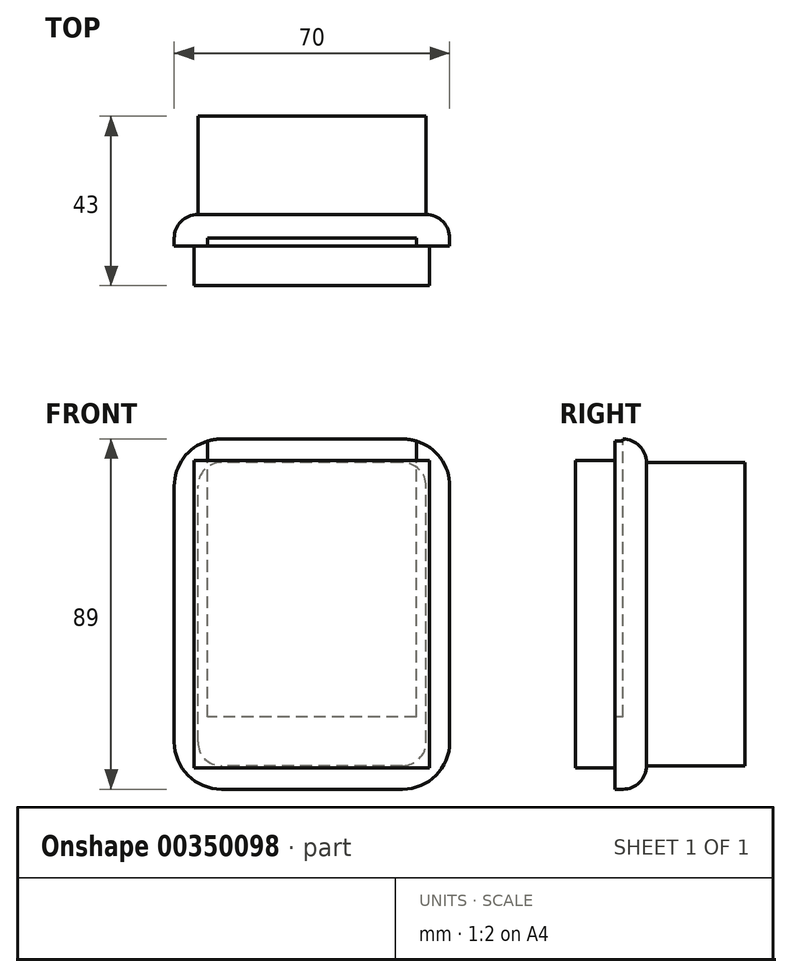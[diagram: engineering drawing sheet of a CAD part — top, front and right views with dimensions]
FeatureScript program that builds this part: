
annotation { "Feature Type Name" : "Feature", "Feature Type Description" : "" }
export const myFeature = defineFeature(function(context is Context, id is Id, definition is map)
    precondition{}
    {
        {
            var Q0;
            Q0=qCreatedBy(makeId("Front.planeOp"),FACE);
            var sketch = newSketch(context, id + "F0", { "sketchPlane" : qUnion([Q0])});
            skLineSegment(sketch, "E0.bottom", {"start": v(889, -1245.88) * mm, "end": v(-889, -1245.88) * mm});
            skLineSegment(sketch, "E0.top", {"start": v(889, 1245.88) * mm, "end": v(-889, 1245.88) * mm});
            skLineSegment(sketch, "E0.left", {"start": v(889, -1245.88) * mm, "end": v(889, 1245.88) * mm});
            skLineSegment(sketch, "E0.right", {"start": v(-889, -1245.88) * mm, "end": v(-889, 1245.88) * mm});
            skPoint(sketch, "E0.middle", {"position": v(0, 0) * mm});
            skLineSegment(sketch, "E1.bottom", {"start": v(35, -44.5) * mm, "end": v(-35, -44.5) * mm});
            skLineSegment(sketch, "E1.top", {"start": v(35, 44.5) * mm, "end": v(-35, 44.5) * mm});
            skLineSegment(sketch, "E1.left", {"start": v(35, -44.5) * mm, "end": v(35, 44.5) * mm});
            skLineSegment(sketch, "E1.right", {"start": v(-35, -44.5) * mm, "end": v(-35, 44.5) * mm});
            skSolve(sketch);
        }
        {
            var Q0;
            Q0=makeQuery(id+"F0.imprint","IMPRINT",FACE,{"disambiguationData":[TD([[makeQuery(id+"F0.imprint","IMPRINT",EDGE,{"derivedFrom":sQuery(id+"F0.wireOp",EDGE,"E1.bottom")}),-1.0]])]});
            extrude(context, id + "F1", {"entities" : qUnion([Q0]), "oppositeDirection" : true, "depth" : 8 * mm});
        }
        {
            var Q0;
            Q0=makeQuery(id+"F1.opExtrude","SWEPT_EDGE",EDGE,{"disambiguationData":[OSD([sQuery(id+"F0.wireOp",EDGE,"E1.top"),sQuery(id+"F0.wireOp",EDGE,"E1.right")])]});
            var Q1;
            Q1=makeQuery(id+"F1.opExtrude","SWEPT_EDGE",EDGE,{"disambiguationData":[OSD([sQuery(id+"F0.wireOp",EDGE,"E1.top"),sQuery(id+"F0.wireOp",EDGE,"E1.left")])]});
            var Q2;
            Q2=makeQuery(id+"F1.opExtrude","SWEPT_EDGE",EDGE,{"disambiguationData":[OSD([sQuery(id+"F0.wireOp",EDGE,"E1.bottom"),sQuery(id+"F0.wireOp",EDGE,"E1.right")])]});
            var Q3;
            Q3=makeQuery(id+"F1.opExtrude","SWEPT_EDGE",EDGE,{"disambiguationData":[OSD([sQuery(id+"F0.wireOp",EDGE,"E1.bottom"),sQuery(id+"F0.wireOp",EDGE,"E1.left")])]});
            fillet(context, id + "F2", {"entities" : qUnion([Q0, Q1, Q2, Q3]), "radius" : 12 * mm, "tangentPropagation" : true, "allowEdgeOverflow" : false});
        }
        {
            var Q0;
            Q0=makeQuery(id+"F1.opExtrude","CAP_EDGE",EDGE,{"disambiguationData":[OSD([sQuery(id+"F0.wireOp",EDGE,"E1.top")])],"isStart":false});
            var Q1;
            {var subQ0=sQuery(id+"F0.wireOp",EDGE,"E1.left");var subQ1=sQuery(id+"F0.wireOp",EDGE,"E1.top");Q1=makeQuery(id+"F2.opFillet","BLEND_EDGE",EDGE,{"blendedFrom":[makeQuery(id+"F1.opExtrude","SWEPT_EDGE",EDGE,{"disambiguationData":[OSD([subQ1,subQ0])]}),makeQuery(id+"F1.opExtrude","CAP_FACE",FACE,{"disambiguationData":[OSD([sQuery(id+"F0.wireOp",EDGE,"E1.bottom"),subQ1,subQ0,sQuery(id+"F0.wireOp",EDGE,"E1.right")])],"isStart":false})],"blendedInto":[makeQuery(id+"F1.opExtrude","CAP_FACE",FACE,{"disambiguationData":[OSD([sQuery(id+"F0.wireOp",EDGE,"E1.bottom"),subQ1,subQ0,sQuery(id+"F0.wireOp",EDGE,"E1.right")])],"isStart":false})]});}
            var Q2;
            Q2=makeQuery(id+"F1.opExtrude","CAP_EDGE",EDGE,{"disambiguationData":[OSD([sQuery(id+"F0.wireOp",EDGE,"E1.left")])],"isStart":false});
            var Q3;
            {var subQ0=sQuery(id+"F0.wireOp",EDGE,"E1.left");var subQ1=sQuery(id+"F0.wireOp",EDGE,"E1.bottom");Q3=makeQuery(id+"F2.opFillet","BLEND_EDGE",EDGE,{"blendedFrom":[makeQuery(id+"F1.opExtrude","SWEPT_EDGE",EDGE,{"disambiguationData":[OSD([subQ1,subQ0])]}),makeQuery(id+"F1.opExtrude","CAP_FACE",FACE,{"disambiguationData":[OSD([subQ1,sQuery(id+"F0.wireOp",EDGE,"E1.top"),subQ0,sQuery(id+"F0.wireOp",EDGE,"E1.right")])],"isStart":false})],"blendedInto":[makeQuery(id+"F1.opExtrude","CAP_FACE",FACE,{"disambiguationData":[OSD([subQ1,sQuery(id+"F0.wireOp",EDGE,"E1.top"),subQ0,sQuery(id+"F0.wireOp",EDGE,"E1.right")])],"isStart":false})]});}
            var Q4;
            Q4=makeQuery(id+"F1.opExtrude","CAP_EDGE",EDGE,{"disambiguationData":[OSD([sQuery(id+"F0.wireOp",EDGE,"E1.bottom")])],"isStart":false});
            var Q5;
            {var subQ0=sQuery(id+"F0.wireOp",EDGE,"E1.right");var subQ1=sQuery(id+"F0.wireOp",EDGE,"E1.bottom");Q5=makeQuery(id+"F2.opFillet","BLEND_EDGE",EDGE,{"blendedFrom":[makeQuery(id+"F1.opExtrude","SWEPT_EDGE",EDGE,{"disambiguationData":[OSD([subQ1,subQ0])]}),makeQuery(id+"F1.opExtrude","CAP_FACE",FACE,{"disambiguationData":[OSD([subQ1,sQuery(id+"F0.wireOp",EDGE,"E1.top"),sQuery(id+"F0.wireOp",EDGE,"E1.left"),subQ0])],"isStart":false})],"blendedInto":[makeQuery(id+"F1.opExtrude","CAP_FACE",FACE,{"disambiguationData":[OSD([subQ1,sQuery(id+"F0.wireOp",EDGE,"E1.top"),sQuery(id+"F0.wireOp",EDGE,"E1.left"),subQ0])],"isStart":false})]});}
            var Q6;
            Q6=makeQuery(id+"F1.opExtrude","CAP_EDGE",EDGE,{"disambiguationData":[OSD([sQuery(id+"F0.wireOp",EDGE,"E1.right")])],"isStart":false});
            var Q7;
            {var subQ0=sQuery(id+"F0.wireOp",EDGE,"E1.right");var subQ1=sQuery(id+"F0.wireOp",EDGE,"E1.top");Q7=makeQuery(id+"F2.opFillet","BLEND_EDGE",EDGE,{"blendedFrom":[makeQuery(id+"F1.opExtrude","SWEPT_EDGE",EDGE,{"disambiguationData":[OSD([subQ1,subQ0])]}),makeQuery(id+"F1.opExtrude","CAP_FACE",FACE,{"disambiguationData":[OSD([sQuery(id+"F0.wireOp",EDGE,"E1.bottom"),subQ1,sQuery(id+"F0.wireOp",EDGE,"E1.left"),subQ0])],"isStart":false})],"blendedInto":[makeQuery(id+"F1.opExtrude","CAP_FACE",FACE,{"disambiguationData":[OSD([sQuery(id+"F0.wireOp",EDGE,"E1.bottom"),subQ1,sQuery(id+"F0.wireOp",EDGE,"E1.left"),subQ0])],"isStart":false})]});}
            fillet(context, id + "F3", {"entities" : qUnion([Q0, Q1, Q2, Q3, Q4, Q5, Q6, Q7]), "radius" : 6 * mm, "tangentPropagation" : true, "allowEdgeOverflow" : false});
        }
        {
            var Q0;
            Q0=makeQuery(id+"F1.opExtrude","CAP_FACE",FACE,{"disambiguationData":[OSD([sQuery(id+"F0.wireOp",EDGE,"E1.bottom"),sQuery(id+"F0.wireOp",EDGE,"E1.top"),sQuery(id+"F0.wireOp",EDGE,"E1.left"),sQuery(id+"F0.wireOp",EDGE,"E1.right")])],"isStart":true});
            var sketch = newSketch(context, id + "F4", { "sketchPlane" : qUnion([Q0])});
            skLineSegment(sketch, "E2.bottom", {"start": v(26.5, -26.06) * mm, "end": v(-26.5, -26.06) * mm});
            skLineSegment(sketch, "E2.top", {"start": v(26.5, 115.06) * mm, "end": v(-26.5, 115.06) * mm});
            skLineSegment(sketch, "E2.left", {"start": v(26.5, -26.06) * mm, "end": v(26.5, 115.06) * mm});
            skLineSegment(sketch, "E2.right", {"start": v(-26.5, -26.06) * mm, "end": v(-26.5, 115.06) * mm});
            skPoint(sketch, "E2.middle", {"position": v(0, 44.5) * mm});
            skSolve(sketch);
        }
        {
            var Q0;
            Q0 = qSketchRegion(id + "F4", true);
            extrude(context, id + "F5", {"entities" : qUnion([Q0]), "operationType" : NewBodyOperationType.REMOVE, "oppositeDirection" : true, "depth" : 2 * mm});
        }
        {
            var Q0;
            Q0=makeQuery(id+"F1.opExtrude","CAP_FACE",FACE,{"disambiguationData":[OSD([sQuery(id+"F0.wireOp",EDGE,"E1.bottom"),sQuery(id+"F0.wireOp",EDGE,"E1.top"),sQuery(id+"F0.wireOp",EDGE,"E1.left"),sQuery(id+"F0.wireOp",EDGE,"E1.right")])],"isStart":true});
            var sketch = newSketch(context, id + "F6", { "sketchPlane" : qUnion([Q0])});
            skLineSegment(sketch, "E3.bottom", {"start": v(29.9, -39.05) * mm, "end": v(-29.9, -39.05) * mm});
            skLineSegment(sketch, "E3.top", {"start": v(29.9, 39.05) * mm, "end": v(-29.9, 39.05) * mm});
            skLineSegment(sketch, "E3.left", {"start": v(29.9, -39.05) * mm, "end": v(29.9, 39.05) * mm});
            skLineSegment(sketch, "E3.right", {"start": v(-29.9, -39.05) * mm, "end": v(-29.9, 39.05) * mm});
            skPoint(sketch, "E3.middle", {"position": v(0, 0) * mm});
            skSolve(sketch);
        }
        {
            var Q0;
            Q0 = qSketchRegion(id + "F6", true);
            extrude(context, id + "F7", {"entities" : qUnion([Q0]), "depth" : 10 * mm});
        }
        {
            var Q0;
            Q0=makeQuery(id+"F1.opExtrude","CAP_FACE",FACE,{"disambiguationData":[OSD([sQuery(id+"F0.wireOp",EDGE,"E1.bottom"),sQuery(id+"F0.wireOp",EDGE,"E1.top"),sQuery(id+"F0.wireOp",EDGE,"E1.left"),sQuery(id+"F0.wireOp",EDGE,"E1.right")])],"isStart":false});
            extrude(context, id + "F8", {"entities" : qUnion([Q0]), "operationType" : NewBodyOperationType.ADD, "depth" : 25 * mm});
        }
    });
